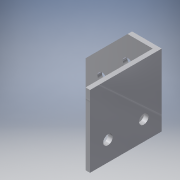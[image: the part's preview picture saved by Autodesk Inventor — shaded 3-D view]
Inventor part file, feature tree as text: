
AUTODESK INVENTOR PART (.ipt)
format: ipt  version: 2016 (Build 200138000, 138)  size: 111,104 bytes
history: native  units: in
note: dims shown in document units (in); Inventor stores cm internally (conversion verified against a paired STEP export)
features: sketch x4, other x3
ambient origin geometry x8: Origin, YZ Plane, XZ Plane, XY Plane, X Axis, Y Axis, Z Axis, Center Point
bodies: Solid1 (feature_tree)
feature tree (7):
  other  "top left rail gusset.ipt"
  other  "Solid1::top left rail gusset.ipt"
  other  "TaggingFeature1"
  sketch  "Sketch1"  dims[d0=0.3937in]
  sketch  "Sketch2"
  sketch  "Sketch3"
  sketch  "Sketch5"
